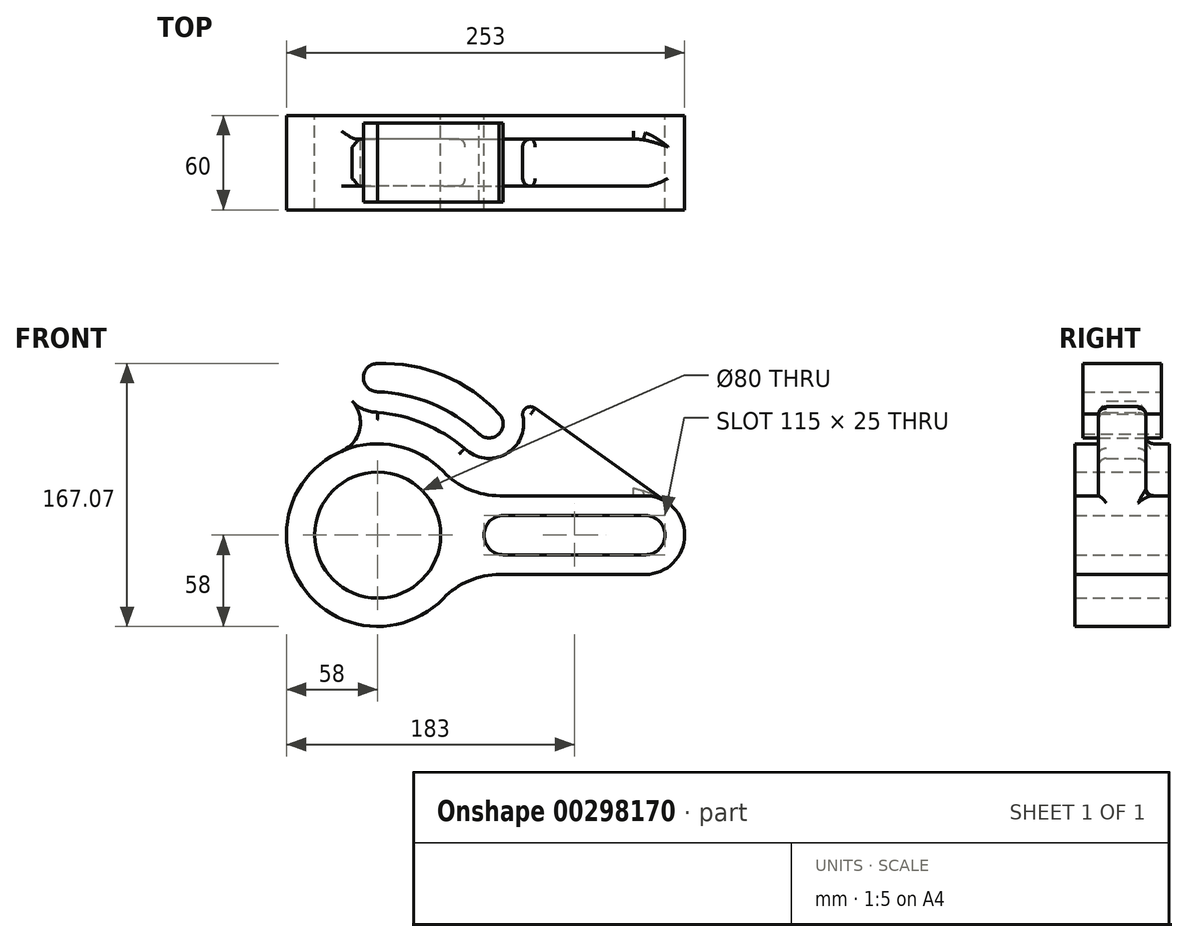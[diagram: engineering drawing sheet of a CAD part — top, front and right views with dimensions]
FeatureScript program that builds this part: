
annotation { "Feature Type Name" : "Feature", "Feature Type Description" : "" }
export const myFeature = defineFeature(function(context is Context, id is Id, definition is map)
    precondition{}
    {
        {
            var Q0;
            Q0=qCreatedBy(makeId("Front.planeOp"),FACE);
            var sketch = newSketch(context, id + "F0", { "sketchPlane" : qUnion([Q0])});
            skCircle(sketch, "E0", {"center": v(0, 0) * mm, "radius": 40 * mm});
            skArc(sketch, "E1", {"start": v(80, -12.5) * mm, "mid": v(67.5, 0) * mm, "end": v(80, 12.5) * mm});
            skArc(sketch, "E2", {"start": v(170, 12.5) * mm, "mid": v(182.5, 0) * mm, "end": v(170, -12.5) * mm});
            skLineSegment(sketch, "E3", {"start": v(80, 12.5) * mm, "end": v(170, 12.5) * mm});
            skLineSegment(sketch, "E4", {"start": v(170, -12.5) * mm, "end": v(80, -12.5) * mm});
            skArc(sketch, "E5", {"start": v(170, -25) * mm, "mid": v(195, 0) * mm, "end": v(170, 25) * mm});
            skArc(sketch, "E6", {"start": v(41.73, 40.28) * mm, "mid": v(-58, 0) * mm, "end": v(41.73, -40.28) * mm});
            skLineSegment(sketch, "E7", {"start": v(77.71, 25) * mm, "end": v(170, 25) * mm});
            skLineSegment(sketch, "E8", {"start": v(77.71, -25) * mm, "end": v(170, -25) * mm});
            skPoint(sketch, "E9.visualSharp", {"position": v(52.34, -25) * mm});
            skArc(sketch, "E9.filletArc", {"start": v(77.71, -25) * mm, "mid": v(58.17, -28.98) * mm, "end": v(41.73, -40.28) * mm});
            skPoint(sketch, "E10.visualSharp", {"position": v(52.34, 25) * mm});
            skArc(sketch, "E10.filletArc", {"start": v(41.73, 40.28) * mm, "mid": v(58.17, 28.98) * mm, "end": v(77.71, 25) * mm});
            skArc(sketch, "E11", {"start": v(-50.74, 86.17) * mm, "mid": v(22.28, 97.49) * mm, "end": v(83.13, 55.58) * mm, "construction": true});
            skArc(sketch, "E12", {"start": v(0, 91) * mm, "mid": v(-9, 100) * mm, "end": v(0, 109) * mm});
            skArc(sketch, "E13", {"start": v(77.07, 77.07) * mm, "mid": v(77.07, 64.35) * mm, "end": v(64.35, 64.35) * mm});
            skLineSegment(sketch, "E14", {"start": v(0, 0) * mm, "end": v(99.35, 99.35) * mm, "construction": true});
            skLineSegment(sketch, "E15", {"start": v(99.35, 99.35) * mm, "end": v(0, 0) * mm, "construction": true});
            skLineSegment(sketch, "E16", {"start": v(0, 0) * mm, "end": v(0, 122) * mm, "construction": true});
            skArc(sketch, "E17", {"start": v(64.35, 64.35) * mm, "mid": v(34.57, 83.46) * mm, "end": v(0, 91) * mm});
            skArc(sketch, "E18", {"start": v(77.07, 77.07) * mm, "mid": v(42.03, 101.46) * mm, "end": v(0, 109) * mm});
            skArc(sketch, "E19", {"start": v(0, 122) * mm, "mid": v(-22, 100) * mm, "end": v(0, 78) * mm});
            skArc(sketch, "E20", {"start": v(55.15, 55.15) * mm, "mid": v(86.27, 55.15) * mm, "end": v(86.27, 86.27) * mm});
            skArc(sketch, "E21", {"start": v(86.27, 86.27) * mm, "mid": v(47.56, 114.82) * mm, "end": v(0, 122) * mm});
            skArc(sketch, "E22", {"start": v(55.15, 55.15) * mm, "mid": v(29.32, 70.79) * mm, "end": v(0, 78) * mm});
            skArc(sketch, "E23", {"start": v(-23, 53.24) * mm, "mid": v(-11.38, 67.43) * mm, "end": v(-16.2, 85.12) * mm});
            skLineSegment(sketch, "E24", {"start": v(67.33, 103.87) * mm, "end": v(184.5, 20.36) * mm});
            skSolve(sketch);
        }
        {
            var Q0;
            Q0=makeQuery(id+"F0.imprint","IMPRINT",FACE,{"disambiguationData":[TD([[makeQuery(id+"F0.imprint","IMPRINT",EDGE,{"derivedFrom":sQuery(id+"F0.wireOp",EDGE,"E0")}),-1.0]])]});
            extrude(context, id + "F1", {"entities" : qUnion([Q0]), "endBound" : BoundingType.SYMMETRIC, "depth" : 60 * mm});
        }
        {
            var Q0;
            Q0=makeQuery(id+"F0.imprint","IMPRINT",FACE,{"disambiguationData":[TD([[makeQuery(id+"F0.imprint","IMPRINT",EDGE,{"derivedFrom":sQuery(id+"F0.wireOp",EDGE,"E12")}),1.0]])]});
            extrude(context, id + "F2", {"entities" : qUnion([Q0]), "endBound" : BoundingType.SYMMETRIC, "depth" : 50 * mm});
        }
        {
            var Q0;
            {var subQ0=sQuery(id+"F0.wireOp",EDGE,"E7");Q0=makeQuery(id+"F0.imprint","IMPRINT",FACE,{"disambiguationData":[TD([[makeQuery(id+"F0.imprint","IMPRINT",EDGE,{"derivedFrom":subQ0}),1.0]])]});}
            extrude(context, id + "F3", {"entities" : qUnion([Q0]), "operationType" : NewBodyOperationType.ADD, "endBound" : BoundingType.SYMMETRIC, "depth" : 30 * mm});
        }
        {
            var Q0;
            Q0=makeQuery(id+"F3.opExtrude","CAP_EDGE",EDGE,{"disambiguationData":[OSD([sQuery(id+"F0.wireOp",EDGE,"E6")])],"isStart":false});
            var Q1;
            Q1=makeQuery(id+"F3.opExtrude","CAP_EDGE",EDGE,{"disambiguationData":[OSD([sQuery(id+"F0.wireOp",EDGE,"E24")])],"isStart":false});
            var Q2;
            Q2=makeQuery(id+"F3.opExtrude","CAP_EDGE",EDGE,{"disambiguationData":[OSD([sQuery(id+"F0.wireOp",EDGE,"E24")])],"isStart":true});
            var Q3;
            Q3=makeQuery(id+"F3.opExtrude","CAP_EDGE",EDGE,{"disambiguationData":[OSD([sQuery(id+"F0.wireOp",EDGE,"E7")])],"isStart":true});
            fillet(context, id + "F4", {"entities" : qUnion([Q0, Q1, Q2, Q3]), "radius" : 5 * mm, "tangentPropagation" : true, "allowEdgeOverflow" : false});
        }
        {
            var Q0;
            Q0=makeQuery(id+"F3.opExtrude","CAP_EDGE",EDGE,{"disambiguationData":[OSD([sQuery(id+"F0.wireOp",EDGE,"E20")])],"isStart":true});
            var Q1;
            Q1=makeQuery(id+"F3.opExtrude","CAP_EDGE",EDGE,{"disambiguationData":[OSD([sQuery(id+"F0.wireOp",EDGE,"E20")])],"isStart":false});
            fillet(context, id + "F5", {"entities" : qUnion([Q0, Q1]), "radius" : 5 * mm, "tangentPropagation" : true, "allowEdgeOverflow" : false});
        }
        {
            var Q0;
            Q0=makeQuery(id+"F3.opExtrude","CAP_EDGE",EDGE,{"disambiguationData":[OSD([sQuery(id+"F0.wireOp",EDGE,"E22")])],"isStart":false});
            var Q1;
            Q1=makeQuery(id+"F3.opExtrude","CAP_EDGE",EDGE,{"disambiguationData":[OSD([sQuery(id+"F0.wireOp",EDGE,"E19")])],"isStart":false});
            var Q2;
            Q2=makeQuery(id+"F3.opExtrude","CAP_EDGE",EDGE,{"disambiguationData":[OSD([sQuery(id+"F0.wireOp",EDGE,"E19")])],"isStart":true});
            var Q3;
            Q3=makeQuery(id+"F3.opExtrude","CAP_EDGE",EDGE,{"disambiguationData":[OSD([sQuery(id+"F0.wireOp",EDGE,"E22")])],"isStart":true});
            fillet(context, id + "F6", {"entities" : qUnion([Q0, Q1, Q2, Q3]), "radius" : 5 * mm, "tangentPropagation" : true, "allowEdgeOverflow" : false});
        }
    });
